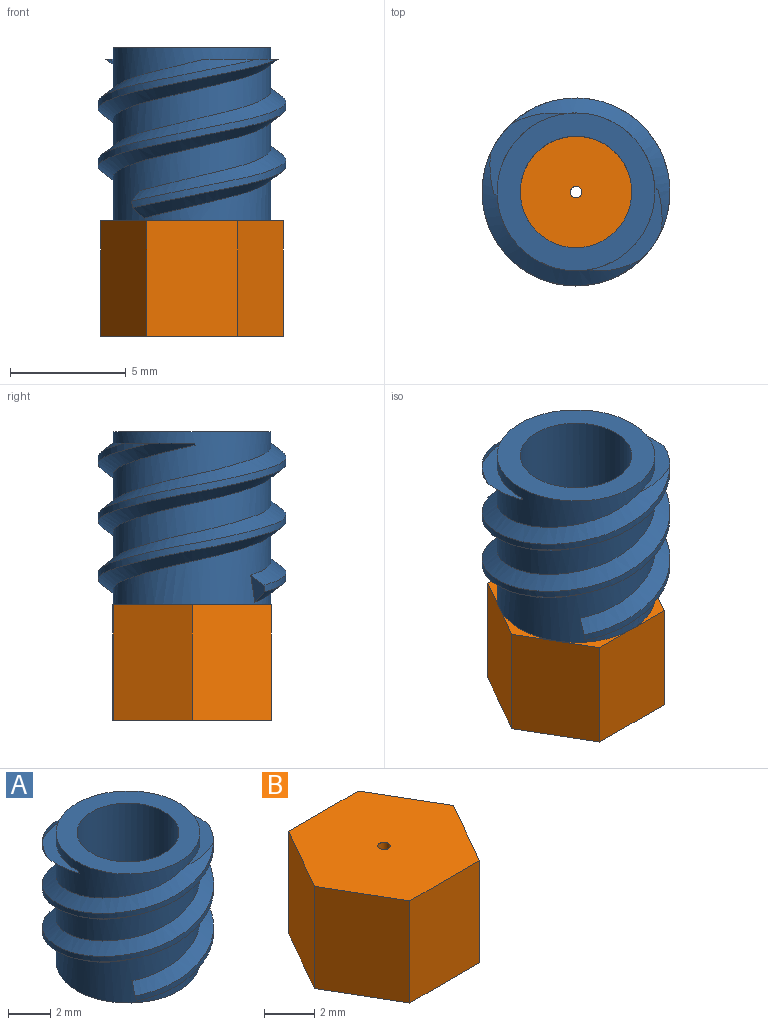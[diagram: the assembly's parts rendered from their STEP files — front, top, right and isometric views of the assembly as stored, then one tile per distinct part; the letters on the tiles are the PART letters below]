
ASSEMBLY  parts=2 mates=1
PART A: 17 faces, bbox 8.3x9.5x7.9 mm
  f0: plane 0.13x0.09mm, normal (0,-0.97,0.23), area 0mm2, adj f3,f9,f15
  f1: bspline ~9.39x8.17mm, area 9.8mm2, adj f2,f3,f12,f15
  f2: bspline ~8.12x8.12mm, area 22.6mm2, adj f1,f8,f9,f12,f15
  f3: bspline ~8.13x8.13mm, area 25.3mm2, adj f0,f1,f8,f9,f12,f15
  f4: plane 0.13x0.09mm, normal (0,0.97,0.23), area 0mm2, adj f7,f9,f14
  f5: bspline ~8.13x8.12mm, area 9.8mm2, adj f6,f7,f13,f14
  f6: bspline ~8.12x8.12mm, area 22.6mm2, adj f5,f8,f9,f13,f14
  f7: bspline ~8.13x8.13mm, area 25.3mm2, adj f4,f5,f8,f9,f13,f14
  f8: cylinder r=3.42mm len=6.89mm, axis (0,0,-1), area 61.9mm2, adj f2,f3,f6,f7,f9,f12,f13,f16
  f9: cylinder r=3.42mm len=6.83mm, axis (0,0,-1), area 32.7mm2, adj f0,f2,f3,f4,f6,f7,f8,f11
  f10: cylinder r=2.42mm len=7.5mm, axis (0,0,-1), area 113.8mm2, adj f11,f16
  f11: plane 6.84x6.84mm, normal (0,0,1), area 18.3mm2, adj f9,f10
  f12: plane 1.18x0.62mm, normal (0.75,-0.62,-0.23), area 0.5mm2, adj f1,f2,f3,f8
  f13: plane 1.18x0.62mm, normal (-0.75,0.62,-0.23), area 0.5mm2, adj f5,f6,f7,f8
  f14: plane 3.62x3.27mm, normal (0,0,1), area 2.3mm2, adj f4,f5,f6,f7,f9
  f15: plane 3.62x3.27mm, normal (0,0,1), area 2.3mm2, adj f0,f1,f2,f3,f9
  f16: plane 6.84x6.84mm, normal (0,0,-1), area 18.3mm2, adj f8,f10
PART B: 13 faces, bbox 7.9x6.8x5 mm
  f0: plane 2x2mm, normal (0,0,-1), area 2.6mm2, adj f4,f5
  f1: plane 0.8x0.8mm, normal (0,0,-1), area 0.3mm2, adj f2,f4
  f2: cylinder r=0.25mm len=0.5mm, axis (0,0,-1), area 0.6mm2, adj f1,f3
  f3: plane 7.89x6.85mm, normal (0,0,1), area 40.2mm2, adj f2,f7,f8,f9,f10,f11,f12
  f4: cylinder r=0.4mm len=0.8mm, axis (0,0,1), area 1.5mm2, adj f0,f1
  f5: cylinder r=1mm len=4mm, axis (0,0,1), area 25.1mm2, adj f0,f6
  f6: plane 7.89x6.85mm, normal (0,0,-1), area 37.3mm2, adj f5,f7,f8,f9,f10,f11,f12
  f7: plane 5x3.94mm, normal (0,-1,0), area 19.7mm2, adj f3,f6,f8,f11
  f8: plane 5x3.41mm, normal (-0.86,-0.5,0), area 19.7mm2, adj f3,f6,f7,f10
  f9: plane 5x3.94mm, normal (0,1,0), area 19.7mm2, adj f3,f6,f10,f12
  f10: plane 5x3.42mm, normal (-0.87,0.5,0), area 19.7mm2, adj f3,f6,f8,f9
  f11: plane 5x3.42mm, normal (0.87,-0.5,0), area 19.7mm2, adj f3,f6,f7,f12
  f12: plane 5x3.41mm, normal (0.86,0.5,0), area 19.7mm2, adj f3,f6,f9,f11
PLACE A t=(-8.97,7.75,-1.34)mm
PLACE B t=(6.03,7.75,2.26)mm
MATE fastened B.f2 <-> A.f10  axis (0,0,1) through (6.03,7.75,2.66)mm
